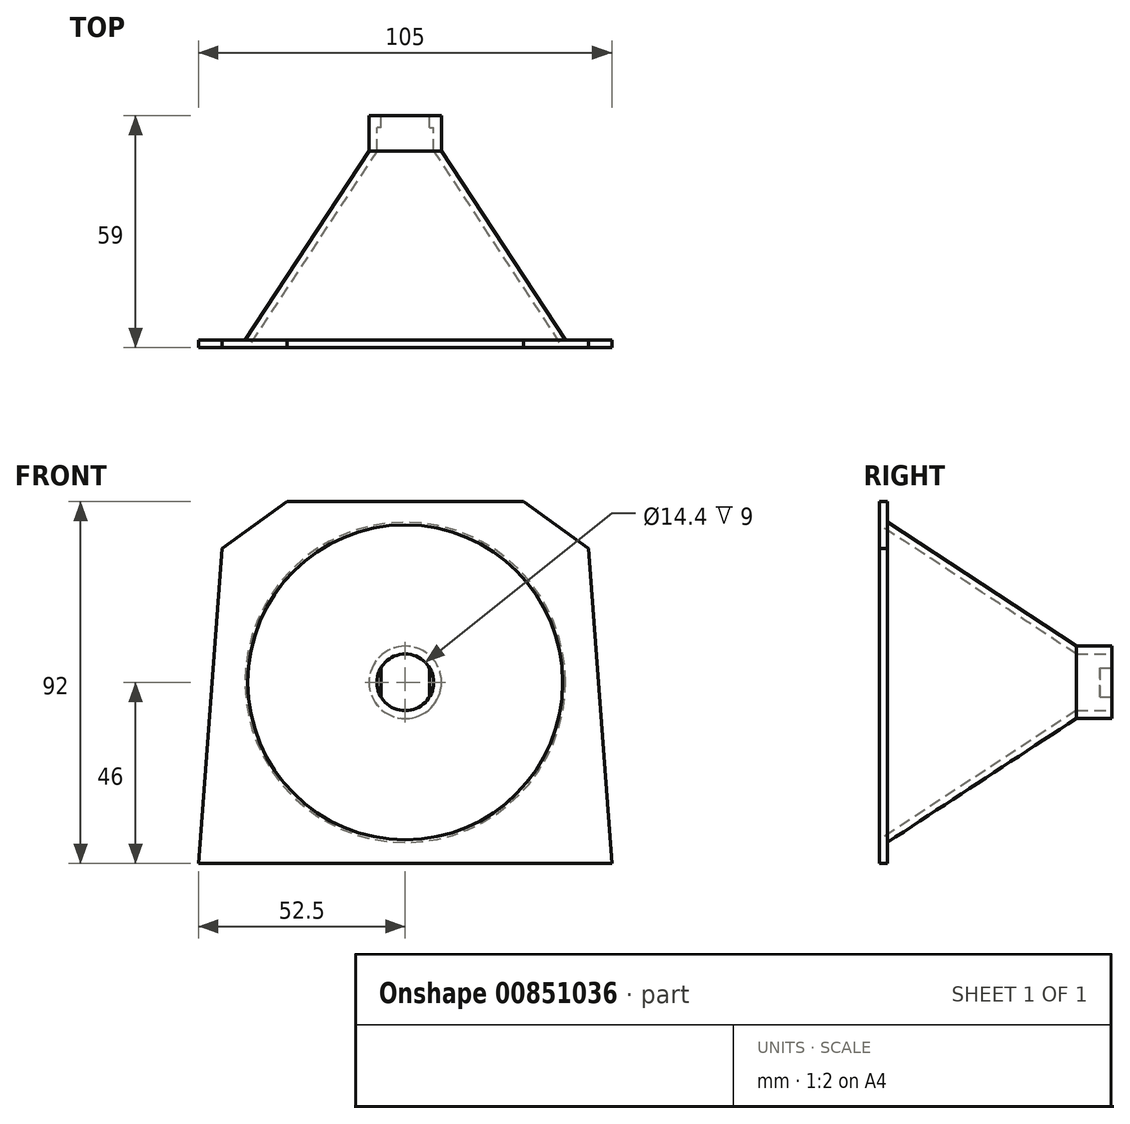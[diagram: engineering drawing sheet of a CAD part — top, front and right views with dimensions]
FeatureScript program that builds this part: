
annotation { "Feature Type Name" : "Feature", "Feature Type Description" : "" }
export const myFeature = defineFeature(function(context is Context, id is Id, definition is map)
    precondition{}
    {
        {
            var Q0;
            Q0=qCreatedBy(makeId("Front.planeOp"),FACE);
            var sketch = newSketch(context, id + "F0", { "sketchPlane" : qUnion([Q0])});
            skLineSegment(sketch, "E0", {"start": v(52.5, -46) * mm, "end": v(-52.5, -46) * mm});
            skLineSegment(sketch, "E1", {"start": v(-46.5, 34) * mm, "end": v(-52.5, -46) * mm});
            skLineSegment(sketch, "E2", {"start": v(46.5, 34) * mm, "end": v(52.5, -46) * mm});
            skLineSegment(sketch, "E3", {"start": v(-30, 46) * mm, "end": v(30, 46) * mm});
            skLineSegment(sketch, "E4", {"start": v(-46.5, 34) * mm, "end": v(-30, 46) * mm});
            skLineSegment(sketch, "E5", {"start": v(30, 46) * mm, "end": v(46.5, 34) * mm});
            skSolve(sketch);
        }
        {
            var Q0;
            Q0=qCreatedBy(makeId("Top.planeOp"),FACE);
            var sketch = newSketch(context, id + "F1", { "sketchPlane" : qUnion([Q0])});
            skLineSegment(sketch, "E6", {"start": v(0, 0) * mm, "end": v(-20, 0) * mm});
            skLineSegment(sketch, "E7", {"start": v(-20, 0) * mm, "end": v(-22, 0) * mm});
            skLineSegment(sketch, "E8", {"start": v(0, 0) * mm, "end": v(-40, 0) * mm});
            skLineSegment(sketch, "E9", {"start": v(0, 0) * mm, "end": v(0, 50) * mm});
            skLineSegment(sketch, "E10", {"start": v(0, 50) * mm, "end": v(-7.2, 50) * mm});
            skLineSegment(sketch, "E11", {"start": v(-7.2, 50) * mm, "end": v(-40, 0) * mm});
            skLineSegment(sketch, "E12", {"start": v(-40, 0) * mm, "end": v(-42, 0) * mm});
            skLineSegment(sketch, "E13", {"start": v(-7.2, 50) * mm, "end": v(-9.2, 50) * mm});
            skLineSegment(sketch, "E14", {"start": v(-9.2, 50) * mm, "end": v(-42, 0) * mm});
            skLineSegment(sketch, "E15", {"start": v(0, 50) * mm, "end": v(0, 59) * mm});
            skLineSegment(sketch, "E16", {"start": v(0, 59) * mm, "end": v(-9.2, 59) * mm});
            skLineSegment(sketch, "E17", {"start": v(-9.2, 59) * mm, "end": v(-9.2, 50) * mm});
            skLineSegment(sketch, "E18", {"start": v(-7.2, 50) * mm, "end": v(-7.2, 59) * mm});
            skSolve(sketch);
        }
        {
            var Q0;
            Q0=makeQuery(id+"F0.imprint","IMPRINT",FACE,{"disambiguationData":[TD([[makeQuery(id+"F0.imprint","IMPRINT",EDGE,{"derivedFrom":sQuery(id+"F0.wireOp",EDGE,"E0")}),-1.0]])]});
            extrude(context, id + "F2", {"entities" : qUnion([Q0]), "oppositeDirection" : true, "depth" : 2 * mm, "offsetDistance" : 25 * mm});
        }
        {
            var Q0;
            {var subQ0=sQuery(id+"F1.wireOp",EDGE,"E9");Q0=makeQuery(id+"F1.imprint","IMPRINT",FACE,{"disambiguationData":[TD([[makeQuery(id+"F1.imprint","IMPRINT",EDGE,{"derivedFrom":subQ0}),1.0]])]});}
            var Q1;
            Q1=sQuery(id+"F1.wireOp",EDGE,"E9");
            revolve(context, id + "F3", {"operationType" : NewBodyOperationType.REMOVE, "surfaceOperationType" : NewSurfaceOperationType.NEW, "entities" : qUnion([Q0]), "axis" : qUnion([Q1]), "revolveType" : RevolveType.FULL, "oppositeDirection" : true});
        }
        {
            var Q0;
            Q0=makeQuery(id+"F1.imprint","IMPRINT",FACE,{"disambiguationData":[TD([[makeQuery(id+"F1.imprint","IMPRINT",EDGE,{"derivedFrom":sQuery(id+"F1.wireOp",EDGE,"E11")}),-1.0]])]});
            var Q1;
            Q1=makeQuery(id+"F1.imprint","IMPRINT",FACE,{"disambiguationData":[TD([[makeQuery(id+"F1.imprint","IMPRINT",EDGE,{"derivedFrom":sQuery(id+"F1.wireOp",EDGE,"E13")}),-1.0]])]});
            var Q2;
            Q2=makeQuery(id+"F3.boolean.opBoolean","INTERSECT",EDGE,{"derivedFrom":[makeQuery(id+"F2.opExtrude","CAP_FACE",FACE,{"disambiguationData":[OSD([sQuery(id+"F0.wireOp",EDGE,"E0"),sQuery(id+"F0.wireOp",EDGE,"E1"),sQuery(id+"F0.wireOp",EDGE,"E2"),sQuery(id+"F0.wireOp",EDGE,"E3"),sQuery(id+"F0.wireOp",EDGE,"E4"),sQuery(id+"F0.wireOp",EDGE,"E5")])],"isStart":false}),makeQuery(id+"F3.opRevolve","SWEPT_FACE",FACE,{"disambiguationData":[OSD([sQuery(id+"F1.wireOp",EDGE,"E11")])]})]});
            revolve(context, id + "F4", {"operationType" : NewBodyOperationType.ADD, "surfaceOperationType" : NewSurfaceOperationType.NEW, "entities" : qUnion([Q0, Q1]), "axis" : qUnion([Q2]), "revolveType" : RevolveType.FULL});
        }
        {
            var Q0;
            Q0=makeQuery(id+"F4.opRevolve","SWEPT_FACE",FACE,{"disambiguationData":[OSD([sQuery(id+"F1.wireOp",EDGE,"E16")])]});
            var sketch = newSketch(context, id + "F5", { "sketchPlane" : qUnion([Q0])});
            skLineSegment(sketch, "E19", {"start": v(0, 0) * mm, "end": v(-6.2, 0) * mm});
            skLineSegment(sketch, "E20", {"start": v(-6.2, 0) * mm, "end": v(-6.2, 3.66) * mm});
            skLineSegment(sketch, "E21", {"start": v(-6.2, 3.66) * mm, "end": v(6.2, 3.66) * mm});
            skLineSegment(sketch, "E22", {"start": v(6.2, 3.66) * mm, "end": v(6.2, -3.66) * mm});
            skLineSegment(sketch, "E23", {"start": v(6.2, -3.66) * mm, "end": v(-6.2, -3.66) * mm});
            skLineSegment(sketch, "E24", {"start": v(-6.2, -3.66) * mm, "end": v(-6.2, 3.66) * mm});
            skSolve(sketch);
        }
        {
            var Q0;
            {var subQ0=sQuery(id+"F5.wireOp",EDGE,"E22");Q0=makeQuery(id+"F5.imprint","IMPRINT",FACE,{"disambiguationData":[TD([[makeQuery(id+"F5.imprint","IMPRINT",EDGE,{"derivedFrom":subQ0}),1.0]])]});}
            var Q1;
            {var subQ0=sQuery(id+"F5.wireOp",EDGE,"E24");var subQ1=makeQuery(id+"F5.imprint","IMPRINT",VERTEX,{"derivedFrom":subQ0});Q1=makeQuery(id+"F5.imprint","IMPRINT",FACE,{"disambiguationData":[TD([[makeQuery(id+"F5.imprint","IMPRINT",EDGE,{"disambiguationData":[TD([[subQ1,1.0]])],"derivedFrom":subQ0}),1.0]])]});}
            extrude(context, id + "F6", {"entities" : qUnion([Q0, Q1]), "operationType" : NewBodyOperationType.ADD, "oppositeDirection" : true, "depth" : 3 * mm, "offsetDistance" : 25 * mm});
        }
    });
